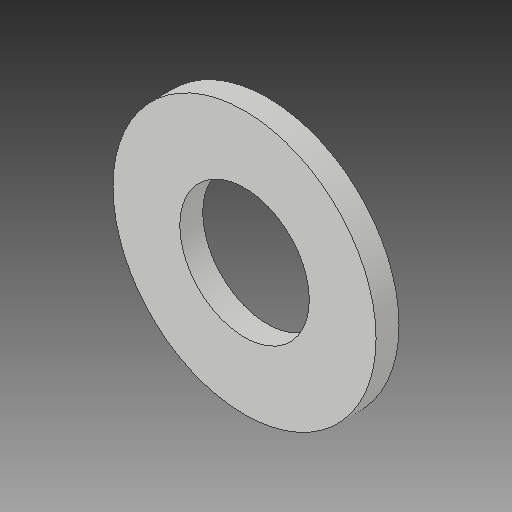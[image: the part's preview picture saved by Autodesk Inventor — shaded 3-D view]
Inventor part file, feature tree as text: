
AUTODESK INVENTOR PART (.ipt)
format: ipt  version: 2018 (Build 220112000, 112)  size: 96,768 bytes
history: native  units: mm
features: other x1, extrude x1, sketch x1
ambient origin geometry x8: Origin, YZ Plane, XZ Plane, XY Plane, X Axis, Y Axis, Z Axis, Center Point
bodies: Body1 (feature_tree)
feature tree (3):
  other  "ソリッド1"
  extrude  "押し出し1"  Depth=25.8mm
  sketch  "スケッチ1"
